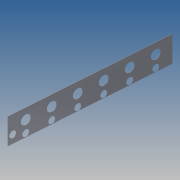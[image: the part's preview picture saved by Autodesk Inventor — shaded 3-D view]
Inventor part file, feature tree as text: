
AUTODESK INVENTOR PART (.ipt)
format: ipt  version: 2014 SP1 (Build 180222100, 222)  size: 180,736 bytes
history: native  units: in
note: dims shown in document units (in); Inventor stores cm internally (conversion verified against a paired STEP export)
features: sketch x7, other x5
ambient origin geometry x8: Origin, YZ Plane, XZ Plane, XY Plane, X Axis, Y Axis, Z Axis, Center Point
bodies: Solid1 (feature_tree)
feature tree (12):
  other  "ringOuter_Split_Flat.ipt"
  other  "Solid1::ringOuter_Split_Flat.ipt"
  other  "TaggingFeature1"
  sketch  "Sketch1"  dims[d0=0.3937in]
  sketch  "Sketch2"  dims[d1=73.1722in d2=10.0in d3=0.0in d5=0.06in d6=3.5433in d7=5.9in d8=5.9624in d9=2.3622in d11=9.4248in d16=3.5433in d23=2.4803in d24=1.3976in d25=2.3622in d27=9.4248in d32=5.9624in d33=2.4803in d40=2.4803in d41=2.4803in d109=2.75in d110=4.7124in d212=0.5in d213=1.0in d214=1.1811in d216=4.0in d221=0.0394in d228=1.25in d230=1.0in d231=0.5in d232=1.1811in d234=4.0in d240=0.0394in d247=0.02in d248=5.9624in d249=0.1in d250=0.0in]
  sketch  "Sketch3"  dims[d177=1.7408in d239=1.5in d255=4.1in d256=8.6024in]
  sketch  "Sketch4"
  sketch  "Sketch19"
  sketch  "Sketch20"
  sketch  "Sketch22"
  other  "Srf1"
  other  "Srf1::Derived"
